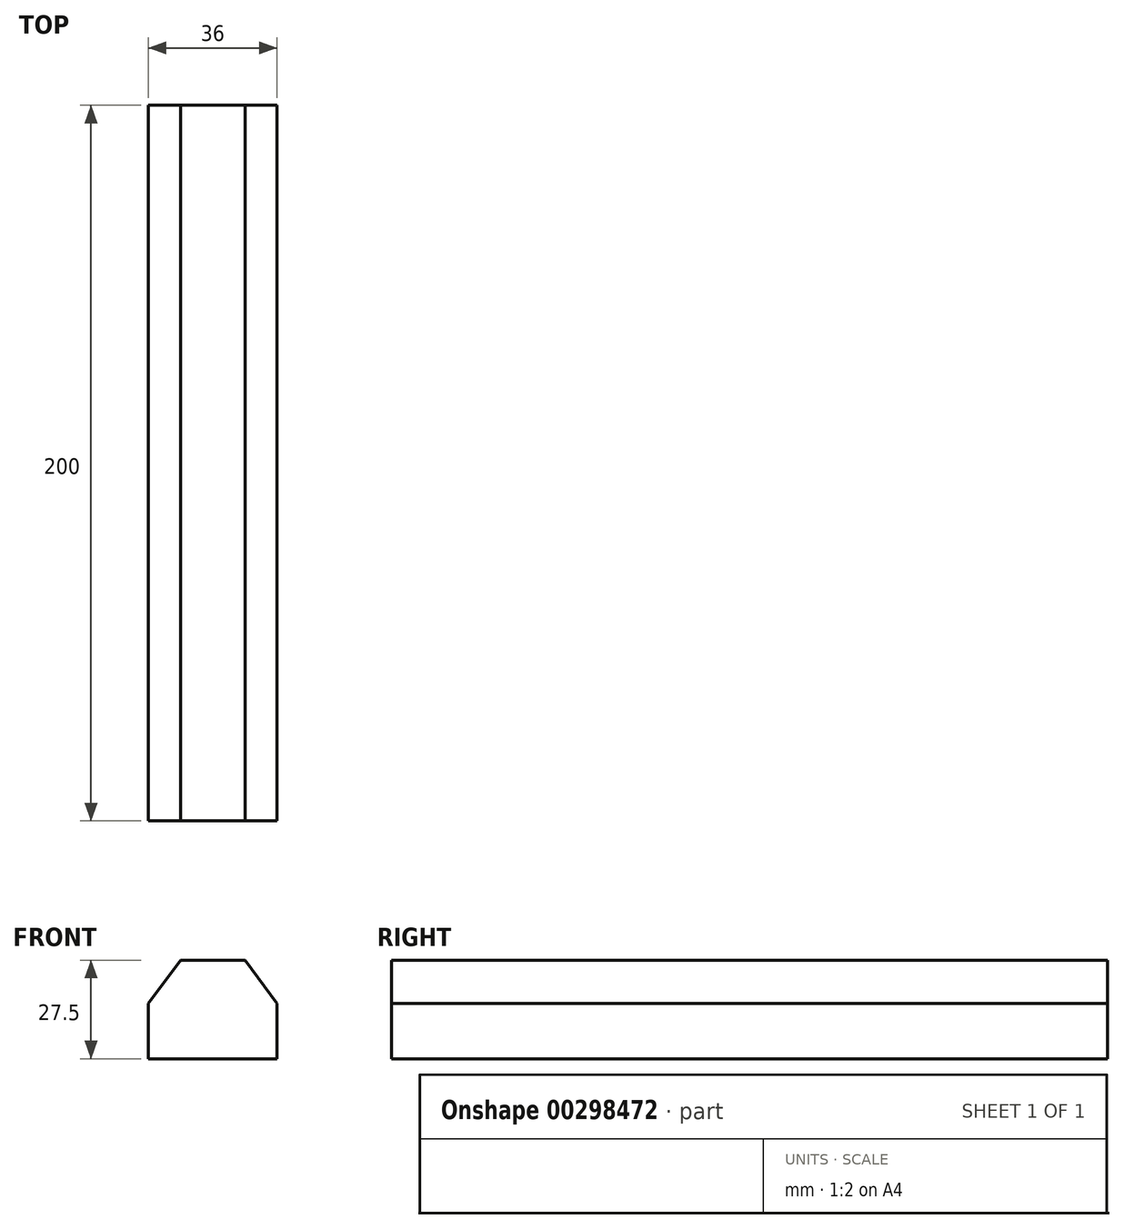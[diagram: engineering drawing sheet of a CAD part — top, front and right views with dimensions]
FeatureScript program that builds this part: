
annotation { "Feature Type Name" : "Feature", "Feature Type Description" : "" }
export const myFeature = defineFeature(function(context is Context, id is Id, definition is map)
    precondition{}
    {
        {
            var Q0;
            Q0=qCreatedBy(makeId("Front.planeOp"),FACE);
            var sketch = newSketch(context, id + "F0", { "sketchPlane" : qUnion([Q0])});
            skLineSegment(sketch, "E0", {"start": v(0, 0) * mm, "end": v(-18, 0) * mm});
            skLineSegment(sketch, "E1", {"start": v(-18, 0) * mm, "end": v(-18, 15.5) * mm});
            skLineSegment(sketch, "E2", {"start": v(-18, 15.5) * mm, "end": v(-9, 27.5) * mm});
            skPoint(sketch, "E2.endSnap0", {"position": v(-9, 0) * mm});
            skLineSegment(sketch, "E3", {"start": v(-9, 27.5) * mm, "end": v(9, 27.5) * mm});
            skLineSegment(sketch, "E4", {"start": v(9, 27.5) * mm, "end": v(18, 15.5) * mm});
            skLineSegment(sketch, "E5", {"start": v(18, 15.5) * mm, "end": v(18, 0) * mm});
            skLineSegment(sketch, "E6", {"start": v(18, 0) * mm, "end": v(0, 0) * mm});
            skSolve(sketch);
        }
        {
            var Q0;
            Q0 = qSketchRegion(id + "F0", true);
            extrude(context, id + "F1", {"entities" : qUnion([Q0]), "depth" : 200 * mm, "offsetDistance" : 25 * mm});
        }
    });
